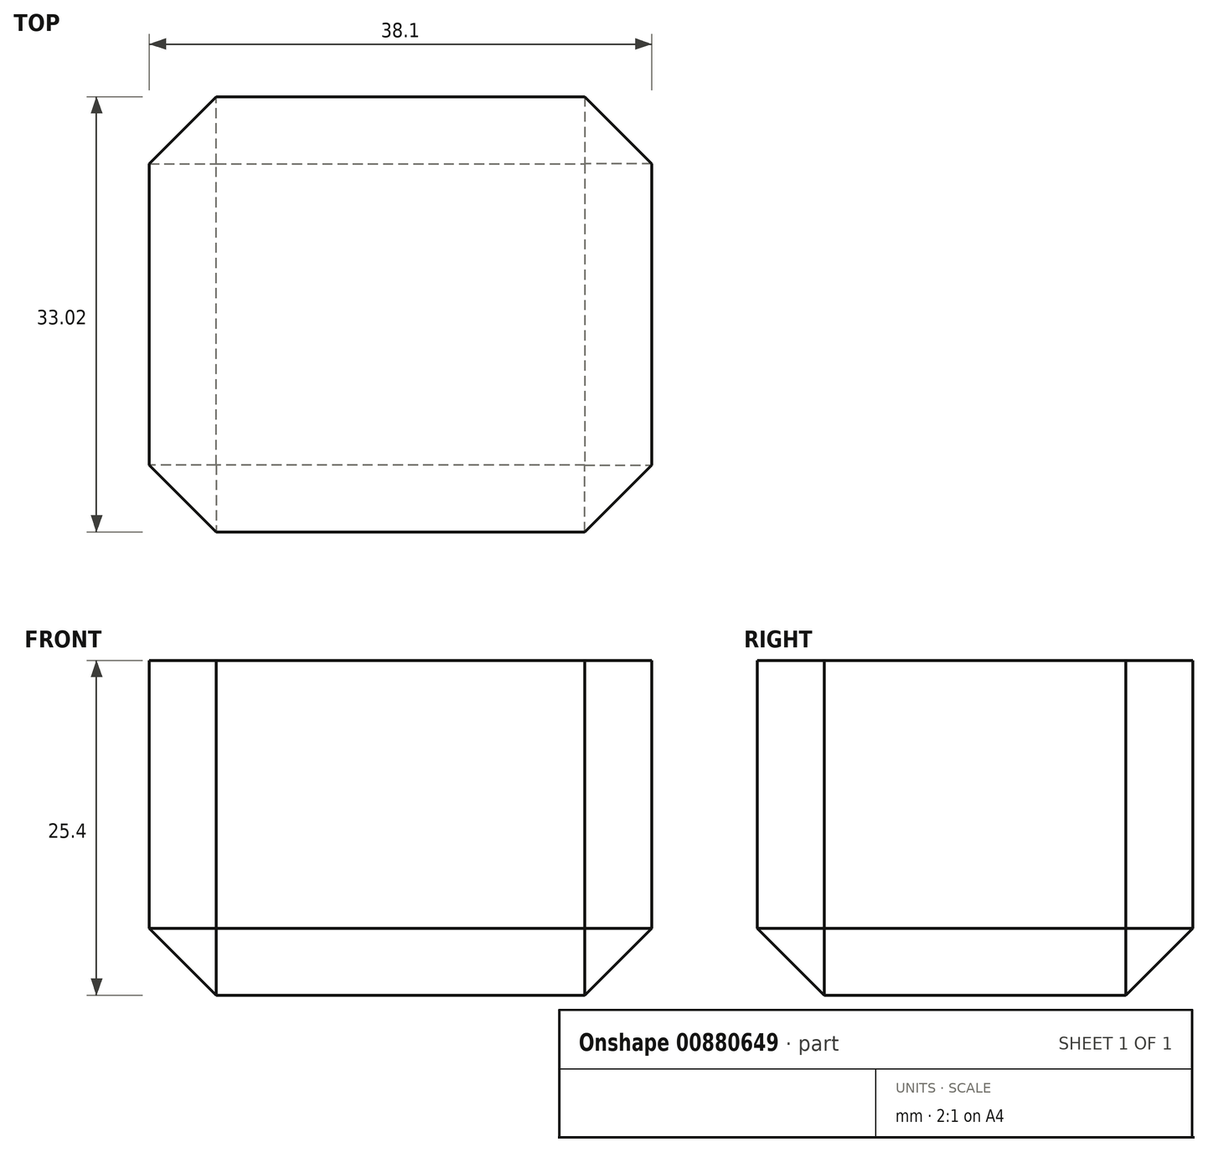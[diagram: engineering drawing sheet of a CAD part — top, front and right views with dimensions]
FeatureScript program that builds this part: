
annotation { "Feature Type Name" : "Feature", "Feature Type Description" : "" }
export const myFeature = defineFeature(function(context is Context, id is Id, definition is map)
    precondition{}
    {
        {
            var Q0;
            Q0=qCreatedBy(makeId("Top.planeOp"),FACE);
            var sketch = newSketch(context, id + "F0", { "sketchPlane" : qUnion([Q0])});
            skLineSegment(sketch, "E0.bottom", {"start": v(0, 0) * mm, "end": v(38.1, 0) * mm});
            skLineSegment(sketch, "E0.top", {"start": v(0, 33.02) * mm, "end": v(38.1, 33.02) * mm});
            skLineSegment(sketch, "E0.left", {"start": v(0, 0) * mm, "end": v(0, 33.02) * mm});
            skLineSegment(sketch, "E0.right", {"start": v(38.1, 0) * mm, "end": v(38.1, 33.02) * mm});
            skSolve(sketch);
        }
        {
            var Q0;
            Q0=makeQuery(id+"F0.imprint","IMPRINT",FACE,{"disambiguationData":[TD([[makeQuery(id+"F0.imprint","IMPRINT",EDGE,{"derivedFrom":sQuery(id+"F0.wireOp",EDGE,"E0.bottom")}),1.0]])]});
            extrude(context, id + "F1", {"entities" : qUnion([Q0]), "oppositeDirection" : true, "depth" : 25.4 * mm, "offsetDistance" : 25.4 * mm});
        }
        {
            var Q0;
            Q0=makeQuery(id+"F1.opExtrude","SWEPT_EDGE",EDGE,{"disambiguationData":[OSD([sQuery(id+"F0.wireOp",EDGE,"E0.bottom"),sQuery(id+"F0.wireOp",EDGE,"E0.right")])]});
            var Q1;
            Q1=makeQuery(id+"F1.opExtrude","SWEPT_EDGE",EDGE,{"disambiguationData":[OSD([sQuery(id+"F0.wireOp",EDGE,"E0.top"),sQuery(id+"F0.wireOp",EDGE,"E0.right")])]});
            var Q2;
            Q2=makeQuery(id+"F1.opExtrude","CAP_EDGE",EDGE,{"disambiguationData":[OSD([sQuery(id+"F0.wireOp",EDGE,"E0.right")])],"isStart":false});
            var Q3;
            Q3=makeQuery(id+"F1.opExtrude","CAP_EDGE",EDGE,{"disambiguationData":[OSD([sQuery(id+"F0.wireOp",EDGE,"E0.bottom")])],"isStart":false});
            var Q4;
            Q4=makeQuery(id+"F1.opExtrude","SWEPT_EDGE",EDGE,{"disambiguationData":[OSD([sQuery(id+"F0.wireOp",EDGE,"E0.bottom"),sQuery(id+"F0.wireOp",EDGE,"E0.left")])]});
            var Q5;
            Q5=makeQuery(id+"F1.opExtrude","CAP_EDGE",EDGE,{"disambiguationData":[OSD([sQuery(id+"F0.wireOp",EDGE,"E0.top")])],"isStart":false});
            var Q6;
            Q6=makeQuery(id+"F1.opExtrude","SWEPT_EDGE",EDGE,{"disambiguationData":[OSD([sQuery(id+"F0.wireOp",EDGE,"E0.top"),sQuery(id+"F0.wireOp",EDGE,"E0.left")])]});
            var Q7;
            Q7=makeQuery(id+"F1.opExtrude","CAP_EDGE",EDGE,{"disambiguationData":[OSD([sQuery(id+"F0.wireOp",EDGE,"E0.left")])],"isStart":false});
            chamfer(context, id + "F2", {"entities" : qUnion([Q0, Q1, Q2, Q3, Q4, Q5, Q6, Q7]), "width" : 5.08 * mm, "tangentPropagation" : true});
        }
    });
